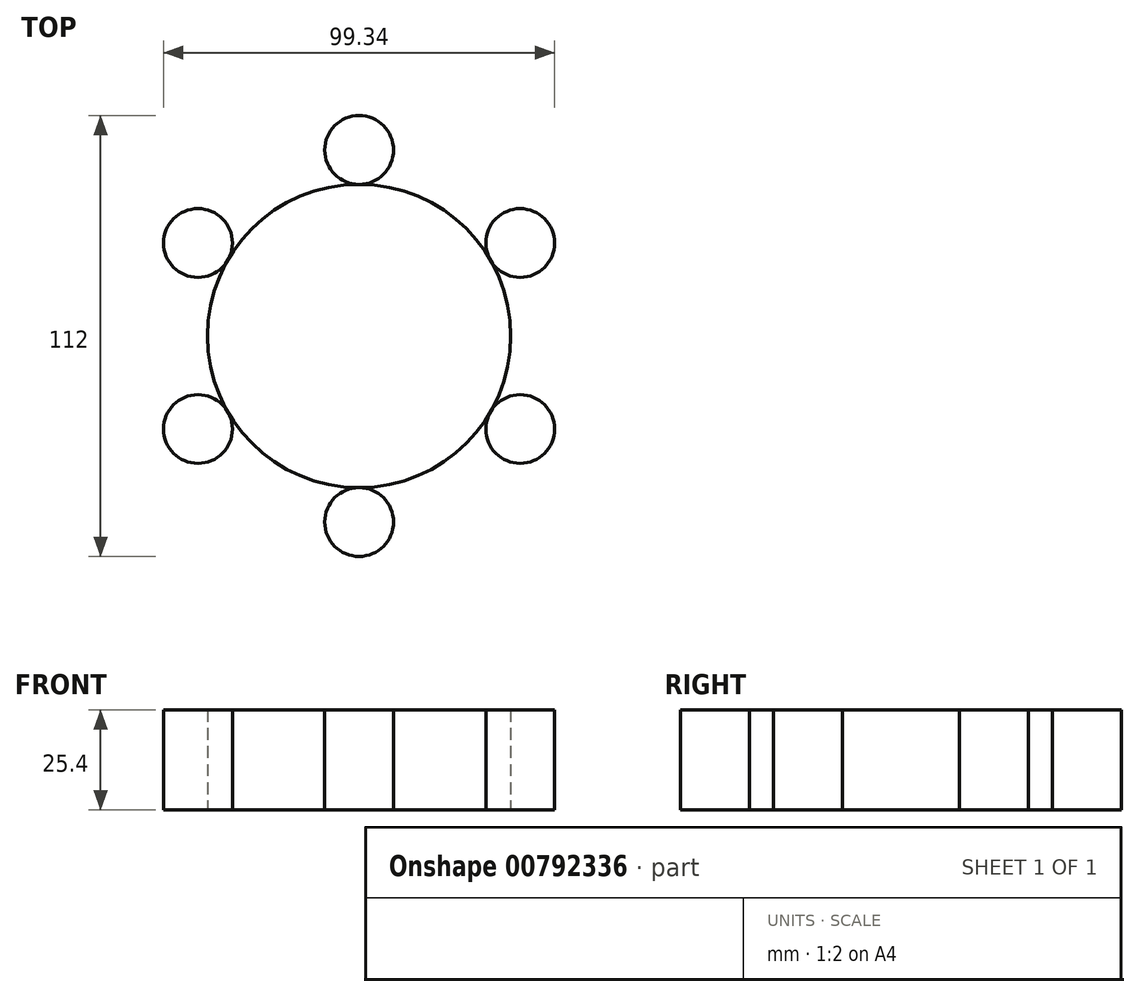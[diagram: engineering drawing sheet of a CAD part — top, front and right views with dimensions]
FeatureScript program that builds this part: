
annotation { "Feature Type Name" : "Feature", "Feature Type Description" : "" }
export const myFeature = defineFeature(function(context is Context, id is Id, definition is map)
    precondition{}
    {
        {
            var Q0;
            Q0=qCreatedBy(makeId("Top.planeOp"),FACE);
            var sketch = newSketch(context, id + "F0", { "sketchPlane" : qUnion([Q0])});
            skCircle(sketch, "E0", {"center": v(0, 0) * mm, "radius": 38.52 * mm});
            skCircle(sketch, "E1", {"center": v(0, 47.26) * mm, "radius": 8.74 * mm});
            skCircle(sketch, "E2.1.0", {"center": v(-40.93, 23.63) * mm, "radius": 8.74 * mm});
            skCircle(sketch, "E2.2.0", {"center": v(-40.93, -23.63) * mm, "radius": 8.74 * mm});
            skCircle(sketch, "E2.3.0", {"center": v(0, -47.26) * mm, "radius": 8.74 * mm});
            skCircle(sketch, "E2.4.0", {"center": v(40.93, -23.63) * mm, "radius": 8.74 * mm});
            skCircle(sketch, "E2.5.0", {"center": v(40.93, 23.63) * mm, "radius": 8.74 * mm});
            skSolve(sketch);
        }
        {
            var Q0;
            Q0=makeQuery(id+"F0.imprint","IMPRINT",FACE,{"disambiguationData":[TD([[makeQuery(id+"F0.imprint","IMPRINT",EDGE,{"derivedFrom":sQuery(id+"F0.wireOp",EDGE,"E1")}),1.0]])]});
            var Q1;
            {var subQ0=sQuery(id+"F0.wireOp",EDGE,"E0");var subQ4=makeQuery(id+"F0.imprint","INTERSECT",VERTEX,{"derivedFrom":[subQ0,sQuery(id+"F0.wireOp",EDGE,"E1")]});Q1=makeQuery(id+"F0.imprint","IMPRINT",FACE,{"disambiguationData":[TD([[makeQuery(id+"F0.imprint","IMPRINT",EDGE,{"disambiguationData":[TD([[subQ4,1.0]])],"derivedFrom":subQ0}),1.0]])]});}
            var Q2;
            Q2=makeQuery(id+"F0.imprint","IMPRINT",FACE,{"disambiguationData":[TD([[makeQuery(id+"F0.imprint","IMPRINT",EDGE,{"derivedFrom":sQuery(id+"F0.wireOp",EDGE,"E2.5.0")}),1.0]])]});
            var Q3;
            Q3=makeQuery(id+"F0.imprint","IMPRINT",FACE,{"disambiguationData":[TD([[makeQuery(id+"F0.imprint","IMPRINT",EDGE,{"derivedFrom":sQuery(id+"F0.wireOp",EDGE,"E2.4.0")}),1.0]])]});
            var Q4;
            Q4=makeQuery(id+"F0.imprint","IMPRINT",FACE,{"disambiguationData":[TD([[makeQuery(id+"F0.imprint","IMPRINT",EDGE,{"derivedFrom":sQuery(id+"F0.wireOp",EDGE,"E2.3.0")}),1.0]])]});
            var Q5;
            Q5=makeQuery(id+"F0.imprint","IMPRINT",FACE,{"disambiguationData":[TD([[makeQuery(id+"F0.imprint","IMPRINT",EDGE,{"derivedFrom":sQuery(id+"F0.wireOp",EDGE,"E2.2.0")}),1.0]])]});
            var Q6;
            Q6=makeQuery(id+"F0.imprint","IMPRINT",FACE,{"disambiguationData":[TD([[makeQuery(id+"F0.imprint","IMPRINT",EDGE,{"derivedFrom":sQuery(id+"F0.wireOp",EDGE,"E2.1.0")}),1.0]])]});
            extrude(context, id + "F1", {"entities" : qUnion([Q0, Q1, Q2, Q3, Q4, Q5, Q6]), "depth" : 25.4 * mm, "offsetDistance" : 25.4 * mm});
        }
    });
